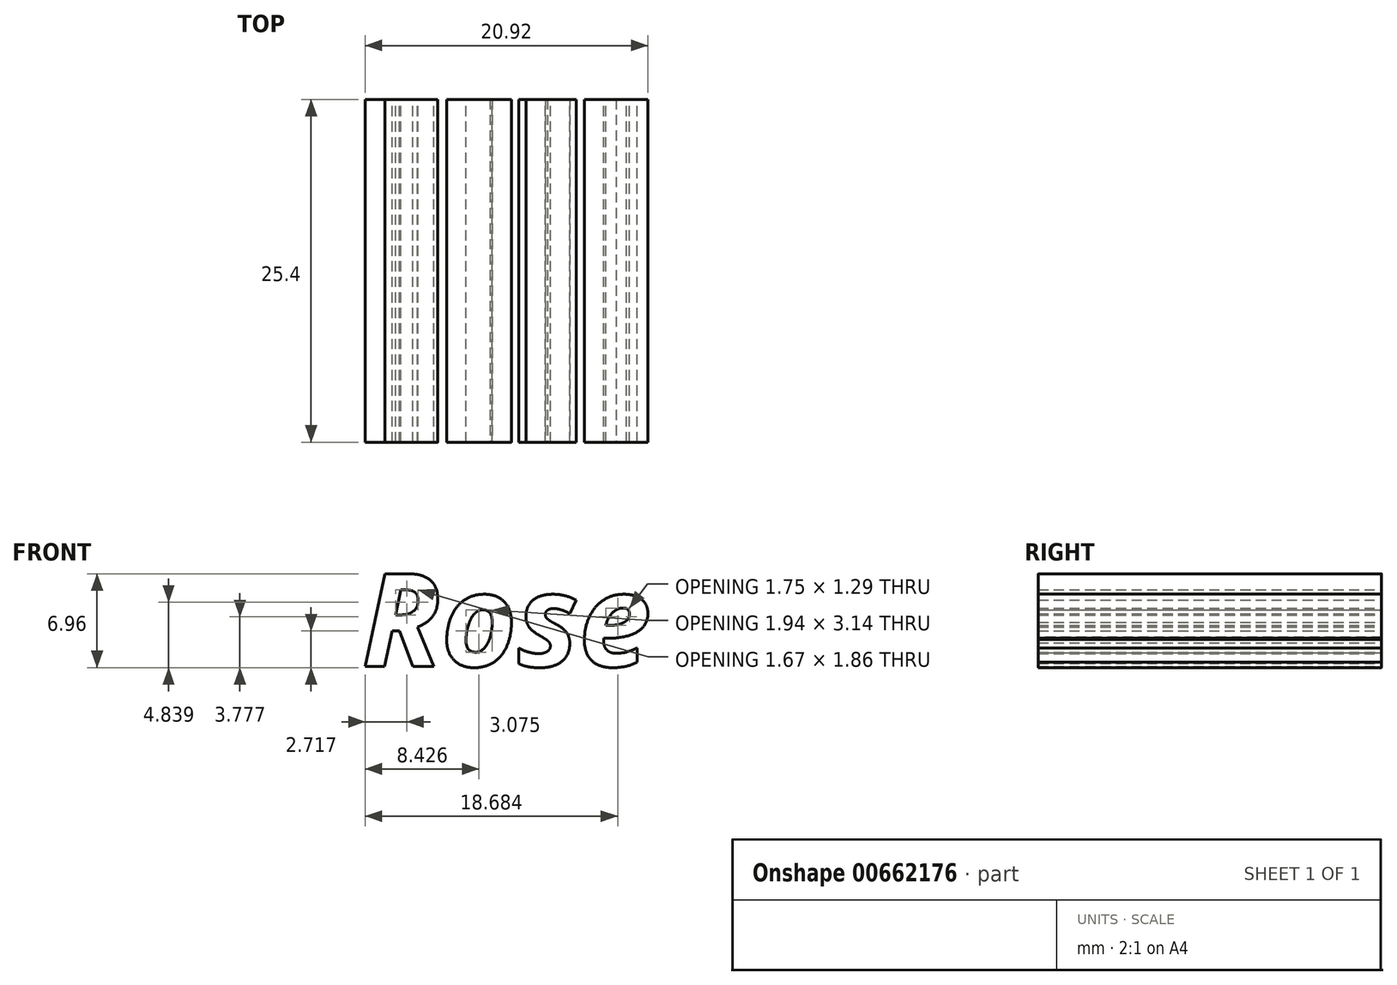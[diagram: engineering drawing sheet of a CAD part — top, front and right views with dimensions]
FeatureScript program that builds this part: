
annotation { "Feature Type Name" : "Feature", "Feature Type Description" : "" }
export const myFeature = defineFeature(function(context is Context, id is Id, definition is map)
    precondition{}
    {
        {
            var Q0;
            Q0=qCreatedBy(makeId("Front.planeOp"),FACE);
            var sketch = newSketch(context, id + "F0", { "sketchPlane" : qUnion([Q0])});
            skText(sketch, "E0", { "text": "Rose\n", "fontName": "OpenSans-BoldItalic.ttf"});
            const initialGuessF0  = {"E0": [-0.0145, 0.00293, 1, 0, 0.00693]};
            skSetInitialGuess(sketch, initialGuessF0);
            skSolve(sketch);
        }
        {
            var Q0;
            Q0 = qSketchRegion(id + "F0", true);
            extrude(context, id + "F1", {"entities" : qUnion([Q0]), "depth" : 25.4 * mm, "offsetDistance" : 25.4 * mm});
        }
    });
